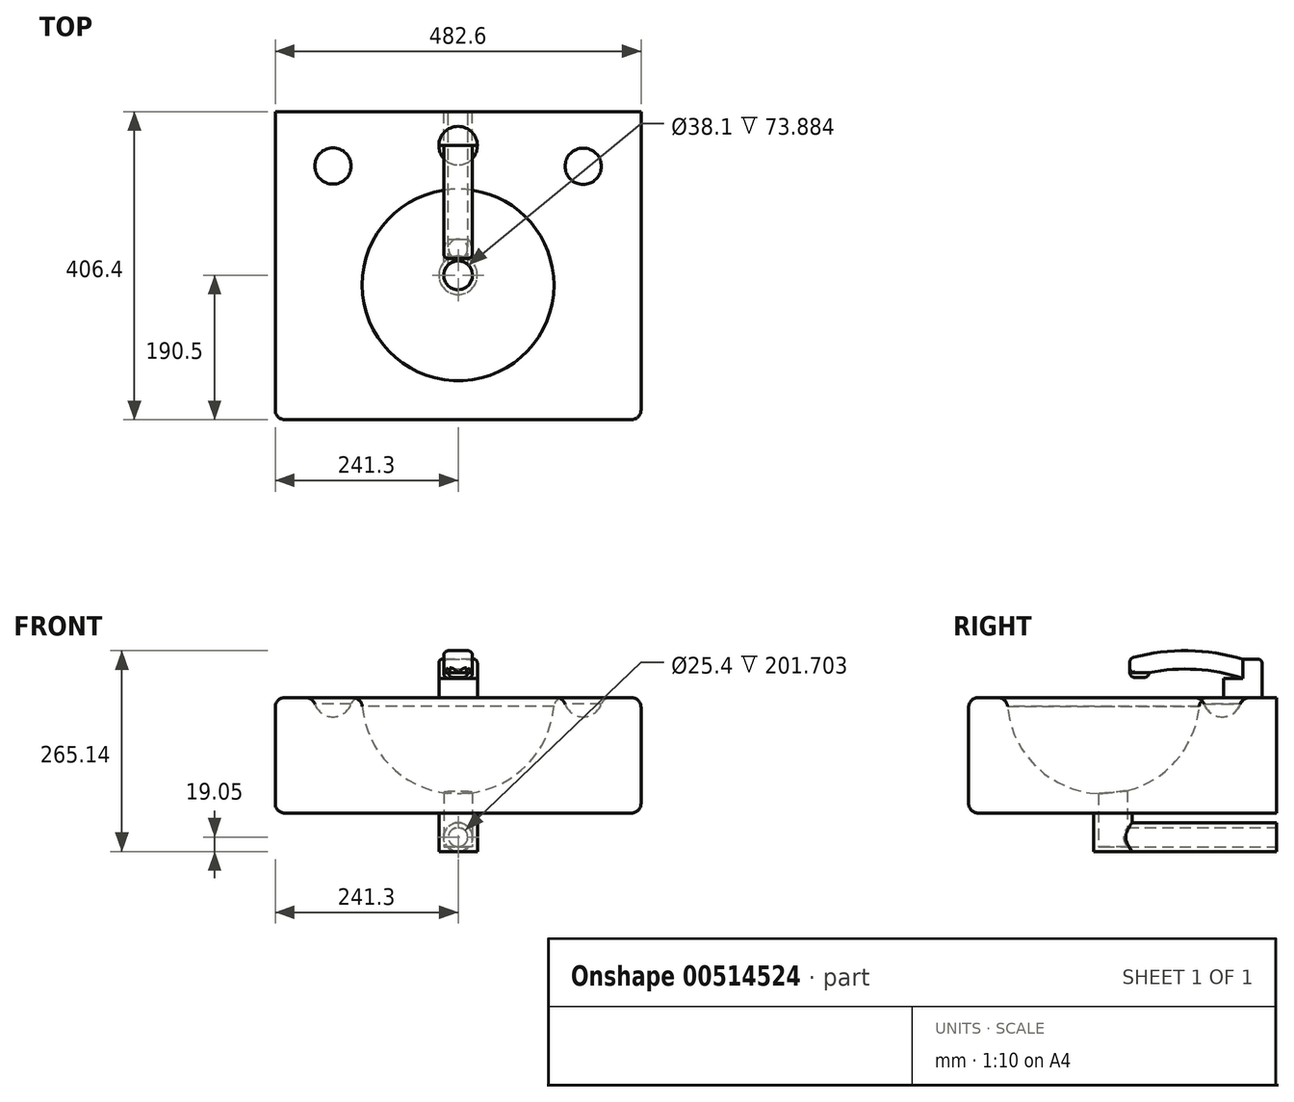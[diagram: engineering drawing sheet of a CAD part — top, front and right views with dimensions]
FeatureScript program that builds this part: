
annotation { "Feature Type Name" : "Feature", "Feature Type Description" : "" }
export const myFeature = defineFeature(function(context is Context, id is Id, definition is map)
    precondition{}
    {
        {
            var Q0;
            Q0=qCreatedBy(makeId("Top.planeOp"),FACE);
            var sketch = newSketch(context, id + "F0", { "sketchPlane" : qUnion([Q0])});
            skLineSegment(sketch, "E0.bottom", {"start": v(241.3, 203.2) * mm, "end": v(-241.3, 203.2) * mm});
            skLineSegment(sketch, "E0.top", {"start": v(241.3, -203.2) * mm, "end": v(-241.3, -203.2) * mm});
            skLineSegment(sketch, "E0.left", {"start": v(241.3, 203.2) * mm, "end": v(241.3, -203.2) * mm});
            skLineSegment(sketch, "E0.right", {"start": v(-241.3, 203.2) * mm, "end": v(-241.3, -203.2) * mm});
            skPoint(sketch, "E0.middle", {"position": v(0, 0) * mm});
            skSolve(sketch);
        }
        {
            var Q0;
            Q0=makeQuery(id+"F0.imprint","IMPRINT",FACE,{"disambiguationData":[TD([[makeQuery(id+"F0.imprint","IMPRINT",EDGE,{"derivedFrom":sQuery(id+"F0.wireOp",EDGE,"E0.bottom")}),1.0]])]});
            extrude(context, id + "F1", {"entities" : qUnion([Q0]), "depth" : 152.4 * mm, "offsetDistance" : 25.4 * mm});
        }
        {
            var Q0;
            Q0=makeQuery(id+"F1.opExtrude","CAP_FACE",FACE,{"disambiguationData":[OSD([sQuery(id+"F0.wireOp",EDGE,"E0.bottom"),sQuery(id+"F0.wireOp",EDGE,"E0.top"),sQuery(id+"F0.wireOp",EDGE,"E0.left"),sQuery(id+"F0.wireOp",EDGE,"E0.right")])],"isStart":false});
            var sketch = newSketch(context, id + "F2", { "sketchPlane" : qUnion([Q0])});
            skLineSegment(sketch, "E1", {"start": v(0, 101.6) * mm, "end": v(0, -25.4) * mm});
            skLineSegment(sketch, "E2", {"start": v(0, -25.4) * mm, "end": v(0, -152.4) * mm});
            skArc(sketch, "E3", {"start": v(0, -152.4) * mm, "mid": v(127, -25.4) * mm, "end": v(0, 101.6) * mm});
            skSolve(sketch);
        }
        {
            var Q0;
            Q0=makeQuery(id+"F2.imprint","IMPRINT",FACE,{"disambiguationData":[TD([[makeQuery(id+"F2.imprint","IMPRINT",EDGE,{"derivedFrom":sQuery(id+"F2.wireOp",EDGE,"E1")}),1.0]])]});
            var Q1;
            Q1=sQuery(id+"F2.wireOp",EDGE,"E1");
            revolve(context, id + "F3", {"operationType" : NewBodyOperationType.REMOVE, "entities" : qUnion([Q0]), "axis" : qUnion([Q1]), "revolveType" : RevolveType.FULL, "oppositeDirection" : true});
        }
        {
            var Q0;
            Q0=makeQuery(id+"F1.opExtrude","CAP_FACE",FACE,{"disambiguationData":[OSD([sQuery(id+"F0.wireOp",EDGE,"E0.bottom"),sQuery(id+"F0.wireOp",EDGE,"E0.top"),sQuery(id+"F0.wireOp",EDGE,"E0.left"),sQuery(id+"F0.wireOp",EDGE,"E0.right")])],"isStart":false});
            var sketch = newSketch(context, id + "F4", { "sketchPlane" : qUnion([Q0])});
            skLineSegment(sketch, "E4", {"start": v(-165.1, 157) * mm, "end": v(-165.1, 106.2) * mm});
            skLineSegment(sketch, "E5", {"start": v(165.1, 156.58) * mm, "end": v(165.1, 105.78) * mm});
            skArc(sketch, "E6", {"start": v(-165.1, 157) * mm, "mid": v(-190.5, 131.6) * mm, "end": v(-165.1, 106.2) * mm});
            skArc(sketch, "E7", {"start": v(165.1, 105.78) * mm, "mid": v(190.5, 131.18) * mm, "end": v(165.1, 156.58) * mm});
            skSolve(sketch);
        }
        {
            var Q0;
            Q0=makeQuery(id+"F4.imprint","IMPRINT",FACE,{"disambiguationData":[TD([[makeQuery(id+"F4.imprint","IMPRINT",EDGE,{"derivedFrom":sQuery(id+"F4.wireOp",EDGE,"E4")}),-1.0]])]});
            var Q1;
            Q1=sQuery(id+"F4.wireOp",EDGE,"E4");
            revolve(context, id + "F5", {"operationType" : NewBodyOperationType.REMOVE, "entities" : qUnion([Q0]), "axis" : qUnion([Q1]), "revolveType" : RevolveType.FULL, "oppositeDirection" : true});
        }
        {
            var Q0;
            Q0=makeQuery(id+"F4.imprint","IMPRINT",FACE,{"disambiguationData":[TD([[makeQuery(id+"F4.imprint","IMPRINT",EDGE,{"derivedFrom":sQuery(id+"F4.wireOp",EDGE,"E5")}),1.0]])]});
            var Q1;
            Q1=sQuery(id+"F4.wireOp",EDGE,"E5");
            revolve(context, id + "F6", {"operationType" : NewBodyOperationType.REMOVE, "entities" : qUnion([Q0]), "axis" : qUnion([Q1]), "revolveType" : RevolveType.FULL, "oppositeDirection" : true});
        }
        {
            var Q0;
            Q0=makeQuery(id+"F3.boolean.opBoolean","INTERSECT",EDGE,{"derivedFrom":[makeQuery(id+"F1.opExtrude","CAP_FACE",FACE,{"disambiguationData":[OSD([sQuery(id+"F0.wireOp",EDGE,"E0.bottom"),sQuery(id+"F0.wireOp",EDGE,"E0.top"),sQuery(id+"F0.wireOp",EDGE,"E0.left"),sQuery(id+"F0.wireOp",EDGE,"E0.right")])],"isStart":false}),makeQuery(id+"F3.opRevolve","SWEPT_FACE",FACE,{"disambiguationData":[OSD([sQuery(id+"F2.wireOp",EDGE,"E3")])]})]});
            var Q1;
            Q1=makeQuery(id+"F5.boolean.opBoolean","INTERSECT",EDGE,{"derivedFrom":[makeQuery(id+"F1.opExtrude","CAP_FACE",FACE,{"disambiguationData":[OSD([sQuery(id+"F0.wireOp",EDGE,"E0.bottom"),sQuery(id+"F0.wireOp",EDGE,"E0.top"),sQuery(id+"F0.wireOp",EDGE,"E0.left"),sQuery(id+"F0.wireOp",EDGE,"E0.right")])],"isStart":false}),makeQuery(id+"F5.opRevolve","SWEPT_FACE",FACE,{"disambiguationData":[OSD([sQuery(id+"F4.wireOp",EDGE,"E6")])]})]});
            var Q2;
            Q2=makeQuery(id+"F6.boolean.opBoolean","INTERSECT",EDGE,{"derivedFrom":[makeQuery(id+"F1.opExtrude","CAP_FACE",FACE,{"disambiguationData":[OSD([sQuery(id+"F0.wireOp",EDGE,"E0.bottom"),sQuery(id+"F0.wireOp",EDGE,"E0.top"),sQuery(id+"F0.wireOp",EDGE,"E0.left"),sQuery(id+"F0.wireOp",EDGE,"E0.right")])],"isStart":false}),makeQuery(id+"F6.opRevolve","SWEPT_FACE",FACE,{"disambiguationData":[OSD([sQuery(id+"F4.wireOp",EDGE,"E7")])]})]});
            var Q3;
            Q3=makeQuery(id+"F1.opExtrude","CAP_EDGE",EDGE,{"disambiguationData":[OSD([sQuery(id+"F0.wireOp",EDGE,"E0.right")])],"isStart":false});
            var Q4;
            Q4=makeQuery(id+"F1.opExtrude","SWEPT_FACE",FACE,{"disambiguationData":[OSD([sQuery(id+"F0.wireOp",EDGE,"E0.top")])]});
            var Q5;
            Q5=makeQuery(id+"F1.opExtrude","CAP_EDGE",EDGE,{"disambiguationData":[OSD([sQuery(id+"F0.wireOp",EDGE,"E0.right")])],"isStart":true});
            var Q6;
            Q6=makeQuery(id+"F1.opExtrude","CAP_EDGE",EDGE,{"disambiguationData":[OSD([sQuery(id+"F0.wireOp",EDGE,"E0.left")])],"isStart":true});
            var Q7;
            Q7=makeQuery(id+"F1.opExtrude","CAP_EDGE",EDGE,{"disambiguationData":[OSD([sQuery(id+"F0.wireOp",EDGE,"E0.left")])],"isStart":false});
            fillet(context, id + "F7", {"entities" : qUnion([Q0, Q1, Q2, Q3, Q4, Q5, Q6, Q7]), "radius" : 12.7 * mm, "tangentPropagation" : true, "allowEdgeOverflow" : false});
        }
        {
            var Q0;
            Q0=makeQuery(id+"F1.opExtrude","CAP_FACE",FACE,{"disambiguationData":[OSD([sQuery(id+"F0.wireOp",EDGE,"E0.bottom"),sQuery(id+"F0.wireOp",EDGE,"E0.top"),sQuery(id+"F0.wireOp",EDGE,"E0.left"),sQuery(id+"F0.wireOp",EDGE,"E0.right")])],"isStart":false});
            var sketch = newSketch(context, id + "F8", { "sketchPlane" : qUnion([Q0])});
            skCircle(sketch, "E8", {"center": v(0, 158.46) * mm, "radius": 25.4 * mm});
            skLineSegment(sketch, "E9", {"start": v(0, 113.72) * mm, "end": v(0, 158.46) * mm});
            skLineSegment(sketch, "E10", {"start": v(0, 203.2) * mm, "end": v(0, 158.46) * mm});
            skSolve(sketch);
        }
        {
            var Q0;
            {var subQ0=sQuery(id+"F8.wireOp",EDGE,"E9");var subQ1=sQuery(id+"F8.wireOp",EDGE,"E8");var subQ2=makeQuery(id+"F8.imprint","INTERSECT",VERTEX,{"derivedFrom":[subQ1,subQ0]});Q0=makeQuery(id+"F8.imprint","IMPRINT",FACE,{"disambiguationData":[TD([[makeQuery(id+"F8.imprint","IMPRINT",EDGE,{"disambiguationData":[TD([[subQ2,1.0]])],"derivedFrom":subQ1}),1.0]])]});}
            var Q1;
            {var subQ0=sQuery(id+"F8.wireOp",EDGE,"E9");var subQ1=sQuery(id+"F8.wireOp",EDGE,"E8");var subQ2=makeQuery(id+"F8.imprint","INTERSECT",VERTEX,{"derivedFrom":[subQ1,subQ0]});Q1=makeQuery(id+"F8.imprint","IMPRINT",FACE,{"disambiguationData":[TD([[makeQuery(id+"F8.imprint","IMPRINT",EDGE,{"disambiguationData":[TD([[subQ2,-1.0]])],"derivedFrom":subQ1}),1.0]])]});}
            extrude(context, id + "F9", {"entities" : qUnion([Q0, Q1]), "operationType" : NewBodyOperationType.ADD, "depth" : 50.8 * mm, "offsetDistance" : 25.4 * mm});
        }
        {
            var Q0;
            Q0=makeQuery(id+"F9.opExtrude","CAP_FACE",FACE,{"disambiguationData":[OSD([sQuery(id+"F8.wireOp",EDGE,"E8")])],"isStart":false});
            var sketch = newSketch(context, id + "F10", { "sketchPlane" : qUnion([Q0])});
            skLineSegment(sketch, "E11.bottom", {"start": v(-25.4, 158.46) * mm, "end": v(25.4, 158.46) * mm});
            skLineSegment(sketch, "E11.top", {"start": v(-25.4, 130.79) * mm, "end": v(25.4, 130.79) * mm});
            skLineSegment(sketch, "E11.left", {"start": v(-25.4, 158.46) * mm, "end": v(-25.4, 130.79) * mm});
            skLineSegment(sketch, "E11.right", {"start": v(25.4, 158.46) * mm, "end": v(25.4, 130.79) * mm});
            skSolve(sketch);
        }
        {
            var Q0;
            {var subQ0=sQuery(id+"F10.wireOp",EDGE,"E11.bottom");Q0=makeQuery(id+"F10.imprint","IMPRINT",FACE,{"disambiguationData":[TD([[makeQuery(id+"F10.imprint","IMPRINT",EDGE,{"derivedFrom":subQ0}),-1.0]])]});}
            extrude(context, id + "F11", {"entities" : qUnion([Q0]), "operationType" : NewBodyOperationType.REMOVE, "oppositeDirection" : true, "depth" : 25.4 * mm, "offsetDistance" : 25.4 * mm});
        }
        {
            var Q0;
            Q0=makeQuery(id+"F1.opExtrude","SWEPT_FACE",FACE,{"disambiguationData":[OSD([sQuery(id+"F0.wireOp",EDGE,"E0.right")])]});
            var sketch = newSketch(context, id + "F12", { "sketchPlane" : qUnion([Q0])});
            skLineSegment(sketch, "E12.0", {"start": v(-158.46, 177.8) * mm, "end": v(-133.06, 177.8) * mm});
            skLineSegment(sketch, "E13.0", {"start": v(-158.46, 177.8) * mm, "end": v(-158.46, 203.2) * mm});
            skArc(sketch, "E14", {"start": v(-6.06, 190.5) * mm, "mid": v(-82.26, 202.2) * mm, "end": v(-158.46, 190.5) * mm});
            skPoint(sketch, "E14.startSnap0", {"position": v(-158.46, 190.5) * mm});
            skSolve(sketch);
        }
        {
            var Q0;
            Q0=makeQuery(id+"F11.boolean.opBoolean","COPY",FACE,{"derivedFrom":makeQuery(id+"F11.opExtrude","SWEPT_FACE",FACE,{"disambiguationData":[OSD([sQuery(id+"F10.wireOp",EDGE,"E11.bottom")])]})});
            var sketch = newSketch(context, id + "F13", { "sketchPlane" : qUnion([Q0])});
            skLineSegment(sketch, "E15.bottom", {"start": v(-19.05, 203.2) * mm, "end": v(19.05, 203.2) * mm});
            skLineSegment(sketch, "E15.top", {"start": v(-19.05, 177.8) * mm, "end": v(19.05, 177.8) * mm});
            skLineSegment(sketch, "E15.left", {"start": v(-19.05, 203.2) * mm, "end": v(-19.05, 177.8) * mm});
            skLineSegment(sketch, "E15.right", {"start": v(19.05, 203.2) * mm, "end": v(19.05, 177.8) * mm});
            skSolve(sketch);
        }
        {
            var Q0;
            Q0=makeQuery(id+"F13.imprint","IMPRINT",FACE,{"disambiguationData":[TD([[makeQuery(id+"F13.imprint","IMPRINT",EDGE,{"derivedFrom":sQuery(id+"F13.wireOp",EDGE,"E15.bottom")}),-1.0]])]});
            var Q1;
            Q1=sQuery(id+"F12.wireOp",EDGE,"E14");
            sweep(context, id + "F14", {"operationType" : NewBodyOperationType.ADD, "profiles" : qUnion([Q0]), "path" : qUnion([Q1])});
        }
        {
            var Q0;
            Q0=makeQuery(id+"F14.opSweep","SWEPT_FACE",FACE,{"disambiguationData":[OSD([sQuery(id+"F12.wireOp",EDGE,"E14"),sQuery(id+"F13.wireOp",EDGE,"E15.right")])]});
            var sketch = newSketch(context, id + "F15", { "sketchPlane" : qUnion([Q0])});
            skLineSegment(sketch, "E16", {"start": v(34.99, 185.45) * mm, "end": v(9.59, 185.45) * mm});
            skLineSegment(sketch, "E17", {"start": v(9.59, 185.45) * mm, "end": v(9.59, 204.23) * mm});
            skSolve(sketch);
        }
        {
            var Q0;
            {var subQ0=sQuery(id+"F15.wireOp",EDGE,"E17");Q0=makeQuery(id+"F15.imprint","IMPRINT",FACE,{"disambiguationData":[TD([[makeQuery(id+"F15.imprint","IMPRINT",EDGE,{"derivedFrom":subQ0}),1.0]])]});}
            var Q1;
            {var subQ0=sQuery(id+"F15.wireOp",EDGE,"E16");Q1=makeQuery(id+"F15.imprint","IMPRINT",FACE,{"disambiguationData":[TD([[makeQuery(id+"F15.imprint","IMPRINT",EDGE,{"derivedFrom":subQ0}),1.0]])]});}
            extrude(context, id + "F16", {"entities" : qUnion([Q0, Q1]), "operationType" : NewBodyOperationType.REMOVE, "oppositeDirection" : true, "depth" : 50.8 * mm, "offsetDistance" : 25.4 * mm});
        }
        {
            var Q0;
            Q0=makeQuery(id+"F16.boolean.opBoolean","COPY",FACE,{"derivedFrom":makeQuery(id+"F16.opExtrude","SWEPT_FACE",FACE,{"disambiguationData":[OSD([sQuery(id+"F15.wireOp",EDGE,"E16")])]})});
            var sketch = newSketch(context, id + "F17", { "sketchPlane" : qUnion([Q0])});
            skCircle(sketch, "E18", {"center": v(0, -22.29) * mm, "radius": 12.7 * mm});
            skSolve(sketch);
        }
        {
            var Q0;
            {var subQ0=sQuery(id+"F17.wireOp",EDGE,"E18");var subQ2=sQuery(id+"F15.wireOp",EDGE,"E16");var subQ3=sQuery(id+"F13.wireOp",EDGE,"E15.right");var subQ6=makeQuery(id+"F17.imprint","INTERSECT",VERTEX,{"derivedFrom":[makeQuery(id+"F16.boolean.opBoolean","COPY",EDGE,{"derivedFrom":makeQuery(id+"F16.opExtrude","SWEPT_EDGE",EDGE,{"disambiguationData":[OSD([sQuery(id+"F10.wireOp",EDGE,"E11.bottom"),sQuery(id+"F12.wireOp",EDGE,"E14"),sQuery(id+"F13.wireOp",EDGE,"E15.top"),subQ3,subQ2])]})}),subQ0]});Q0=makeQuery(id+"F17.imprint","IMPRINT",FACE,{"disambiguationData":[TD([[makeQuery(id+"F17.imprint","IMPRINT",EDGE,{"disambiguationData":[TD([[subQ6,1.0]])],"derivedFrom":subQ0}),1.0]])]});}
            extrude(context, id + "F18", {"entities" : qUnion([Q0]), "operationType" : NewBodyOperationType.ADD, "depth" : 6.35 * mm, "offsetDistance" : 25.4 * mm});
        }
        {
            var Q0;
            Q0=makeQuery(id+"F18.opExtrude","CAP_FACE",FACE,{"disambiguationData":[OSD([sQuery(id+"F17.wireOp",EDGE,"E18")])],"isStart":false});
            var Q1;
            Q1=makeQuery(id+"F16.boolean.opBoolean","COPY",EDGE,{"derivedFrom":makeQuery(id+"F16.opExtrude","CAP_EDGE",EDGE,{"disambiguationData":[OSD([sQuery(id+"F15.wireOp",EDGE,"E17")])],"isStart":true})});
            var Q2;
            Q2=makeQuery(id+"F16.boolean.opBoolean","COPY",EDGE,{"derivedFrom":makeQuery(id+"F16.opExtrude","SWEPT_EDGE",EDGE,{"disambiguationData":[OSD([sQuery(id+"F10.wireOp",EDGE,"E11.bottom"),sQuery(id+"F12.wireOp",EDGE,"E14"),sQuery(id+"F13.wireOp",EDGE,"E15.bottom"),sQuery(id+"F13.wireOp",EDGE,"E15.right"),sQuery(id+"F15.wireOp",EDGE,"E17")])]})});
            var Q3;
            Q3=makeQuery(id+"F16.boolean.opBoolean","INTERSECT",EDGE,{"derivedFrom":[makeQuery(id+"F14.opSweep","SWEPT_FACE",FACE,{"disambiguationData":[OSD([sQuery(id+"F12.wireOp",EDGE,"E14"),sQuery(id+"F13.wireOp",EDGE,"E15.left")])]}),makeQuery(id+"F16.opExtrude","SWEPT_FACE",FACE,{"disambiguationData":[OSD([sQuery(id+"F15.wireOp",EDGE,"E17")])]})]});
            var Q4;
            Q4=makeQuery(id+"F16.boolean.opBoolean","COPY",FACE,{"derivedFrom":makeQuery(id+"F16.opExtrude","SWEPT_FACE",FACE,{"disambiguationData":[OSD([sQuery(id+"F15.wireOp",EDGE,"E17")])]})});
            var Q5;
            Q5=makeQuery(id+"F14.opSweep","SWEPT_EDGE",EDGE,{"disambiguationData":[OSD([sQuery(id+"F10.wireOp",EDGE,"E11.bottom"),sQuery(id+"F12.wireOp",EDGE,"E14"),sQuery(id+"F13.wireOp",EDGE,"E15.top"),sQuery(id+"F13.wireOp",EDGE,"E15.left")])]});
            var Q6;
            Q6=makeQuery(id+"F14.opSweep","SWEPT_EDGE",EDGE,{"disambiguationData":[OSD([sQuery(id+"F10.wireOp",EDGE,"E11.bottom"),sQuery(id+"F12.wireOp",EDGE,"E14"),sQuery(id+"F13.wireOp",EDGE,"E15.bottom"),sQuery(id+"F13.wireOp",EDGE,"E15.left")])]});
            var Q7;
            Q7=makeQuery(id+"F14.opSweep","SWEPT_EDGE",EDGE,{"disambiguationData":[OSD([sQuery(id+"F10.wireOp",EDGE,"E11.bottom"),sQuery(id+"F12.wireOp",EDGE,"E14"),sQuery(id+"F13.wireOp",EDGE,"E15.top"),sQuery(id+"F13.wireOp",EDGE,"E15.right")])]});
            var Q8;
            Q8=makeQuery(id+"F14.opSweep","SWEPT_EDGE",EDGE,{"disambiguationData":[OSD([sQuery(id+"F10.wireOp",EDGE,"E11.bottom"),sQuery(id+"F12.wireOp",EDGE,"E14"),sQuery(id+"F13.wireOp",EDGE,"E15.bottom"),sQuery(id+"F13.wireOp",EDGE,"E15.right")])]});
            fillet(context, id + "F19", {"entities" : qUnion([Q0, Q1, Q2, Q3, Q4, Q5, Q6, Q7, Q8]), "radius" : 6.35 * mm, "tangentPropagation" : true, "allowEdgeOverflow" : false});
        }
        {
            var Q0;
            Q0=makeQuery(id+"F9.opExtrude","CAP_EDGE",EDGE,{"disambiguationData":[OSD([sQuery(id+"F8.wireOp",EDGE,"E8")])],"isStart":false});
            var Q1;
            Q1=makeQuery(id+"F9.opExtrude","CAP_EDGE",EDGE,{"disambiguationData":[OSD([sQuery(id+"F8.wireOp",EDGE,"E8")])],"isStart":true});
            var Q2;
            Q2=makeQuery(id+"F11.boolean.opBoolean","COPY",EDGE,{"derivedFrom":makeQuery(id+"F11.opExtrude","CAP_EDGE",EDGE,{"disambiguationData":[OSD([sQuery(id+"F8.wireOp",EDGE,"E8")])],"isStart":false})});
            var Q3;
            Q3=makeQuery(id+"F11.boolean.opBoolean","COPY",EDGE,{"derivedFrom":makeQuery(id+"F11.opExtrude","SWEPT_EDGE",EDGE,{"disambiguationData":[OSD([sQuery(id+"F8.wireOp",EDGE,"E8"),sQuery(id+"F10.wireOp",EDGE,"E11.bottom"),sQuery(id+"F10.wireOp",EDGE,"E11.right")])]})});
            var Q4;
            Q4=makeQuery(id+"F11.boolean.opBoolean","COPY",EDGE,{"derivedFrom":makeQuery(id+"F11.opExtrude","SWEPT_EDGE",EDGE,{"disambiguationData":[OSD([sQuery(id+"F8.wireOp",EDGE,"E8"),sQuery(id+"F10.wireOp",EDGE,"E11.bottom"),sQuery(id+"F10.wireOp",EDGE,"E11.left")])]})});
            fillet(context, id + "F20", {"entities" : qUnion([Q0, Q1, Q2, Q3, Q4]), "radius" : 5.08 * mm, "tangentPropagation" : true, "allowEdgeOverflow" : false});
        }
        {
            var Q0;
            Q0=makeQuery(id+"F1.opExtrude","CAP_FACE",FACE,{"disambiguationData":[OSD([sQuery(id+"F0.wireOp",EDGE,"E0.bottom"),sQuery(id+"F0.wireOp",EDGE,"E0.top"),sQuery(id+"F0.wireOp",EDGE,"E0.left"),sQuery(id+"F0.wireOp",EDGE,"E0.right")])],"isStart":true});
            var sketch = newSketch(context, id + "F21", { "sketchPlane" : qUnion([Q0])});
            skCircle(sketch, "E19", {"center": v(0, 12.7) * mm, "radius": 127 * mm});
            skLineSegment(sketch, "E20", {"start": v(0, 139.7) * mm, "end": v(0, 190.5) * mm});
            skCircle(sketch, "E21", {"center": v(0, 12.7) * mm, "radius": 19.05 * mm});
            skSolve(sketch);
        }
        {
            var Q0;
            Q0=makeQuery(id+"F21.imprint","IMPRINT",FACE,{"disambiguationData":[TD([[makeQuery(id+"F21.imprint","IMPRINT",EDGE,{"derivedFrom":sQuery(id+"F21.wireOp",EDGE,"E21")}),1.0]])]});
            extrude(context, id + "F22", {"entities" : qUnion([Q0]), "operationType" : NewBodyOperationType.REMOVE, "oppositeDirection" : true, "depth" : 38.1 * mm, "offsetDistance" : 25.4 * mm});
        }
        {
            var Q0;
            Q0=makeQuery(id+"F1.opExtrude","CAP_FACE",FACE,{"disambiguationData":[OSD([sQuery(id+"F0.wireOp",EDGE,"E0.bottom"),sQuery(id+"F0.wireOp",EDGE,"E0.top"),sQuery(id+"F0.wireOp",EDGE,"E0.left"),sQuery(id+"F0.wireOp",EDGE,"E0.right")])],"isStart":true});
            var sketch = newSketch(context, id + "F23", { "sketchPlane" : qUnion([Q0])});
            skCircle(sketch, "E22", {"center": v(0, 12.7) * mm, "radius": 25.4 * mm});
            skCircle(sketch, "E23", {"center": v(0, 12.7) * mm, "radius": 19.05 * mm});
            skSolve(sketch);
        }
        {
            var Q0;
            Q0=makeQuery(id+"F23.imprint","IMPRINT",FACE,{"disambiguationData":[TD([[makeQuery(id+"F23.imprint","IMPRINT",EDGE,{"derivedFrom":sQuery(id+"F23.wireOp",EDGE,"E22")}),1.0]])]});
            extrude(context, id + "F24", {"entities" : qUnion([Q0]), "operationType" : NewBodyOperationType.ADD, "depth" : 50.8 * mm, "offsetDistance" : 25.4 * mm});
        }
        {
            var Q0;
            Q0=makeQuery(id+"F24.opExtrude","CAP_FACE",FACE,{"disambiguationData":[OSD([sQuery(id+"F23.wireOp",EDGE,"E22"),sQuery(id+"F23.wireOp",EDGE,"E23")])],"isStart":false});
            var sketch = newSketch(context, id + "F25", { "sketchPlane" : qUnion([Q0])});
            skCircle(sketch, "E24.0", {"center": v(0, 12.7) * mm, "radius": 25.4 * mm});
            skSolve(sketch);
        }
        {
            var Q0;
            Q0=makeQuery(id+"F25.imprint","IMPRINT",FACE,{"disambiguationData":[TD([[makeQuery(id+"F25.imprint","IMPRINT",EDGE,{"derivedFrom":makeQuery(id+"F24.opExtrude","CAP_EDGE",EDGE,{"disambiguationData":[OSD([sQuery(id+"F23.wireOp",EDGE,"E23")])],"isStart":false})}),1.0]])]});
            extrude(context, id + "F26", {"entities" : qUnion([Q0]), "operationType" : NewBodyOperationType.ADD, "oppositeDirection" : true, "depth" : 6.35 * mm, "offsetDistance" : 25.4 * mm});
        }
        {
            var Q0;
            Q0=makeQuery(id+"F1.opExtrude","SWEPT_FACE",FACE,{"disambiguationData":[OSD([sQuery(id+"F0.wireOp",EDGE,"E0.bottom")])]});
            var sketch = newSketch(context, id + "F27", { "sketchPlane" : qUnion([Q0])});
            skLineSegment(sketch, "E25.bottom", {"start": v(-25.46, 0) * mm, "end": v(25.34, 0) * mm});
            skLineSegment(sketch, "E25.top", {"start": v(-25.46, -50.8) * mm, "end": v(25.34, -50.8) * mm});
            skLineSegment(sketch, "E25.left", {"start": v(-25.46, 0) * mm, "end": v(-25.46, -50.8) * mm});
            skLineSegment(sketch, "E25.right", {"start": v(25.34, 0) * mm, "end": v(25.34, -50.8) * mm});
            skLineSegment(sketch, "E26.left", {"start": v(-25.46, -50.8) * mm, "end": v(-25.46, -44.45) * mm});
            skLineSegment(sketch, "E26.right", {"start": v(25.34, -50.8) * mm, "end": v(25.34, -44.45) * mm});
            skCircle(sketch, "E27", {"center": v(0, -31.75) * mm, "radius": 12.7 * mm});
            skCircle(sketch, "E28", {"center": v(0, -31.75) * mm, "radius": 19.05 * mm});
            skPoint(sketch, "E29", {"position": v(0, -50.8) * mm});
            skSolve(sketch);
        }
        {
            var Q0;
            Q0=makeQuery(id+"F27.imprint","IMPRINT",FACE,{"disambiguationData":[TD([[makeQuery(id+"F27.imprint","IMPRINT",EDGE,{"derivedFrom":sQuery(id+"F27.wireOp",EDGE,"E27")}),1.0]])]});
            extrude(context, id + "F28", {"entities" : qUnion([Q0]), "operationType" : NewBodyOperationType.REMOVE, "oppositeDirection" : true, "depth" : 203.2 * mm, "offsetDistance" : 25.4 * mm});
        }
        {
            var Q0;
            Q0=makeQuery(id+"F27.imprint","IMPRINT",FACE,{"disambiguationData":[TD([[makeQuery(id+"F27.imprint","IMPRINT",EDGE,{"derivedFrom":sQuery(id+"F27.wireOp",EDGE,"E27")}),-1.0]])]});
            extrude(context, id + "F29", {"entities" : qUnion([Q0]), "operationType" : NewBodyOperationType.ADD, "endBound" : BoundingType.UP_TO_NEXT, "oppositeDirection" : true, "depth" : 196.85 * mm, "offsetDistance" : 25.4 * mm});
        }
    });
